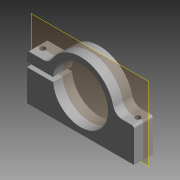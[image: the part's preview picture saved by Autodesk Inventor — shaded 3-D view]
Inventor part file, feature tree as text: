
AUTODESK INVENTOR PART (.ipt)
format: ipt  version: 2013 (Build 170138000, 138)  size: 110,592 bytes
history: native  units: in
note: dims shown in document units (in); Inventor stores cm internally (conversion verified against a paired STEP export)
features: other x3, plane x1
ambient origin geometry x8: Origin, YZ Plane, XZ Plane, XY Plane, X Axis, Y Axis, Z Axis, Center Point
bodies: Solid1 (feature_tree)
feature tree (4):
  other  "Tetrix motor mount.ipt"
  plane  "Work Plane1"
  other  "DC_MOTOR_MOUNT_2011::Tetrix motor mount.ipt"
  other  "TaggingFeature1"
